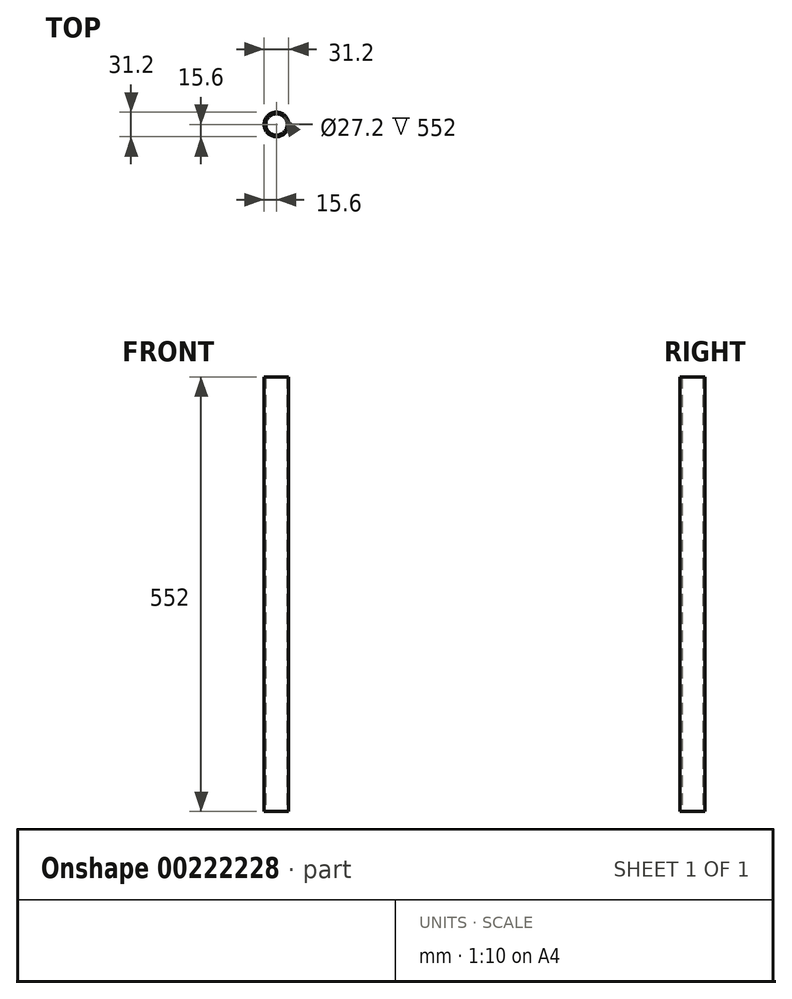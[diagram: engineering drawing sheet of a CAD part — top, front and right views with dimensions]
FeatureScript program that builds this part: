
annotation { "Feature Type Name" : "Feature", "Feature Type Description" : "" }
export const myFeature = defineFeature(function(context is Context, id is Id, definition is map)
    precondition{}
    {
        {
            var Q0;
            Q0=qCreatedBy(makeId("Top.planeOp"),FACE);
            var sketch = newSketch(context, id + "F0", { "sketchPlane" : qUnion([Q0])});
            skCircle(sketch, "E0", {"center": v(0, 0) * mm, "radius": 13.6 * mm});
            skCircle(sketch, "E1.0", {"center": v(0, 0) * mm, "radius": 15.6 * mm});
            skSolve(sketch);
        }
        {
            var Q0;
            Q0 = qSketchRegion(id + "F0", true);
            extrude(context, id + "F1", {"entities" : qUnion([Q0]), "depth" : 552 * mm});
        }
    });
